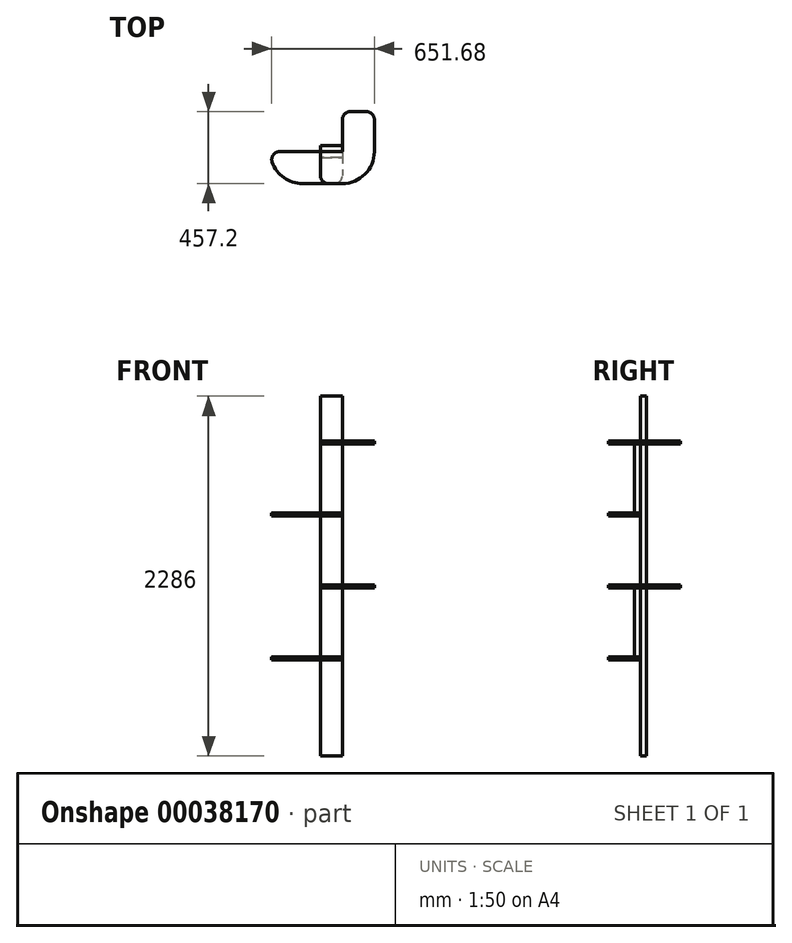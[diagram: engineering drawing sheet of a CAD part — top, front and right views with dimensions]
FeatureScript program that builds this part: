
annotation { "Feature Type Name" : "Feature", "Feature Type Description" : "" }
export const myFeature = defineFeature(function(context is Context, id is Id, definition is map)
    precondition{}
    {
        {
            var Q0;
            Q0=qCreatedBy(makeId("Top.planeOp"),FACE);
            cPlane(context, id + "F0", {"entities" : qUnion([Q0]), "cplaneType" : CPlaneType.OFFSET, "offset" : 609.6 * mm, "width" : 152.4 * mm, "height" : 152.4 * mm});
        }
        {
            var Q0;
            Q0=qCreatedBy(id+"F0.planeOp",FACE);
            cPlane(context, id + "F1", {"entities" : qUnion([Q0]), "cplaneType" : CPlaneType.OFFSET, "offset" : 457.2 * mm, "width" : 152.4 * mm, "height" : 152.4 * mm});
        }
        {
            var Q0;
            Q0=qCreatedBy(id+"F1.planeOp",FACE);
            cPlane(context, id + "F2", {"entities" : qUnion([Q0]), "cplaneType" : CPlaneType.OFFSET, "offset" : 457.2 * mm, "width" : 152.4 * mm, "height" : 152.4 * mm});
        }
        {
            var Q0;
            Q0=qCreatedBy(id+"F2.planeOp",FACE);
            cPlane(context, id + "F3", {"entities" : qUnion([Q0]), "cplaneType" : CPlaneType.OFFSET, "offset" : 457.2 * mm, "width" : 152.4 * mm, "height" : 152.4 * mm});
        }
        {
            var Q0;
            Q0=qCreatedBy(makeId("Top.planeOp"),FACE);
            var sketch = newSketch(context, id + "F4", { "sketchPlane" : qUnion([Q0])});
            skLineSegment(sketch, "E0.bottom", {"start": v(0, 0) * mm, "end": v(-139.7, 0) * mm});
            skLineSegment(sketch, "E0.top", {"start": v(0, 38.1) * mm, "end": v(-139.7, 38.1) * mm});
            skLineSegment(sketch, "E0.left", {"start": v(0, 0) * mm, "end": v(0, 38.1) * mm});
            skLineSegment(sketch, "E0.right", {"start": v(-139.7, 0) * mm, "end": v(-139.7, 38.1) * mm});
            skSolve(sketch);
        }
        {
            var Q0;
            Q0 = qSketchRegion(id + "F4", true);
            extrude(context, id + "F5", {"entities" : qUnion([Q0]), "depth" : 2286 * mm});
        }
        {
            var Q0;
            Q0=qCreatedBy(id+"F0.planeOp",FACE);
            var sketch = newSketch(context, id + "F6", { "sketchPlane" : qUnion([Q0])});
            skLineSegment(sketch, "E1.bottom", {"start": v(0, 0) * mm, "end": v(-254, 0) * mm});
            skLineSegment(sketch, "E1.top", {"start": v(-50.8, -203.2) * mm, "end": v(-254, -203.2) * mm});
            skLineSegment(sketch, "E1.left", {"start": v(0, 0) * mm, "end": v(0, -152.4) * mm});
            skArc(sketch, "E2", {"start": v(-254, -203.2) * mm, "mid": v(-371.32, -165.91) * mm, "end": v(-445.58, -67.73) * mm});
            skLineSegment(sketch, "E3", {"start": v(-397.68, 0) * mm, "end": v(-254, 0) * mm});
            skPoint(sketch, "E4.visualSharp", {"position": v(0, -203.2) * mm});
            skArc(sketch, "E4.filletArc", {"start": v(-50.8, -203.2) * mm, "mid": v(-14.88, -188.32) * mm, "end": v(0, -152.4) * mm});
            skPoint(sketch, "E5.visualSharp", {"position": v(-457.2, 0) * mm});
            skArc(sketch, "E5.filletArc", {"start": v(-397.68, 0) * mm, "mid": v(-439.16, -21.47) * mm, "end": v(-445.58, -67.73) * mm});
            skSolve(sketch);
        }
        {
            var Q0;
            Q0 = qSketchRegion(id + "F6", true);
            extrude(context, id + "F7", {"entities" : qUnion([Q0]), "depth" : 19.05 * mm});
        }
        {
            var Q0;
            Q0=qCreatedBy(id+"F1.planeOp",FACE);
            var sketch = newSketch(context, id + "F8", { "sketchPlane" : qUnion([Q0])});
            skLineSegment(sketch, "E6", {"start": v(-139.7, 0) * mm, "end": v(-139.7, -152.4) * mm});
            skArc(sketch, "E7", {"start": v(-139.7, -152.4) * mm, "mid": v(-124.82, -188.32) * mm, "end": v(-88.9, -203.2) * mm});
            skLineSegment(sketch, "E8", {"start": v(-88.9, -203.2) * mm, "end": v(0, -203.2) * mm});
            skLineSegment(sketch, "E9", {"start": v(203.2, 0) * mm, "end": v(203.2, 203.2) * mm});
            skLineSegment(sketch, "E10", {"start": v(152.4, 254) * mm, "end": v(50.8, 254) * mm});
            skLineSegment(sketch, "E11", {"start": v(0, 203.2) * mm, "end": v(0, 0) * mm});
            skArc(sketch, "E12", {"start": v(0, -203.2) * mm, "mid": v(143.68, -143.68) * mm, "end": v(203.2, 0) * mm});
            skPoint(sketch, "E13.visualSharp", {"position": v(0, 254) * mm});
            skArc(sketch, "E13.filletArc", {"start": v(50.8, 254) * mm, "mid": v(14.88, 239.12) * mm, "end": v(0, 203.2) * mm});
            skPoint(sketch, "E14.visualSharp", {"position": v(203.2, 254) * mm});
            skArc(sketch, "E14.filletArc", {"start": v(203.2, 203.2) * mm, "mid": v(188.32, 239.12) * mm, "end": v(152.4, 254) * mm});
            skLineSegment(sketch, "E15", {"start": v(-139.7, 0) * mm, "end": v(0, 0) * mm});
            skSolve(sketch);
        }
        {
            var Q0;
            Q0 = qSketchRegion(id + "F8", true);
            extrude(context, id + "F9", {"entities" : qUnion([Q0]), "depth" : 19.05 * mm});
        }
        {
            var Q0;
            Q0=qCreatedBy(id+"F2.planeOp",FACE);
            var sketch = newSketch(context, id + "F10", { "sketchPlane" : qUnion([Q0])});
            skLineSegment(sketch, "E16.bottom", {"start": v(0, 0) * mm, "end": v(-254, 0) * mm});
            skLineSegment(sketch, "E16.top", {"start": v(-50.8, -203.2) * mm, "end": v(-254, -203.2) * mm});
            skLineSegment(sketch, "E16.left", {"start": v(0, 0) * mm, "end": v(0, -152.4) * mm});
            skArc(sketch, "E17", {"start": v(-254, -203.2) * mm, "mid": v(-371.32, -165.91) * mm, "end": v(-445.58, -67.73) * mm});
            skLineSegment(sketch, "E18", {"start": v(-397.68, 0) * mm, "end": v(-254, 0) * mm});
            skPoint(sketch, "E19.visualSharp", {"position": v(0, -203.2) * mm});
            skArc(sketch, "E19.filletArc", {"start": v(-50.8, -203.2) * mm, "mid": v(-14.88, -188.32) * mm, "end": v(0, -152.4) * mm});
            skPoint(sketch, "E20.visualSharp", {"position": v(-457.2, 0) * mm});
            skArc(sketch, "E20.filletArc", {"start": v(-397.68, 0) * mm, "mid": v(-439.16, -21.47) * mm, "end": v(-445.58, -67.73) * mm});
            skSolve(sketch);
        }
        {
            var Q0;
            Q0 = qSketchRegion(id + "F10", true);
            extrude(context, id + "F11", {"entities" : qUnion([Q0]), "depth" : 19.05 * mm});
        }
        {
            var Q0;
            Q0=qCreatedBy(id+"F3.planeOp",FACE);
            var sketch = newSketch(context, id + "F12", { "sketchPlane" : qUnion([Q0])});
            skLineSegment(sketch, "E21", {"start": v(-139.7, 0) * mm, "end": v(-139.7, -152.4) * mm});
            skArc(sketch, "E22", {"start": v(-139.7, -152.4) * mm, "mid": v(-124.82, -188.32) * mm, "end": v(-88.9, -203.2) * mm});
            skLineSegment(sketch, "E23", {"start": v(-88.9, -203.2) * mm, "end": v(0, -203.2) * mm});
            skLineSegment(sketch, "E24", {"start": v(203.2, 0) * mm, "end": v(203.2, 203.2) * mm});
            skLineSegment(sketch, "E25", {"start": v(152.4, 254) * mm, "end": v(50.8, 254) * mm});
            skLineSegment(sketch, "E26", {"start": v(0, 203.2) * mm, "end": v(0, 0) * mm});
            skArc(sketch, "E27", {"start": v(0, -203.2) * mm, "mid": v(143.68, -143.68) * mm, "end": v(203.2, 0) * mm});
            skPoint(sketch, "E28.visualSharp", {"position": v(0, 254) * mm});
            skArc(sketch, "E28.filletArc", {"start": v(50.8, 254) * mm, "mid": v(14.88, 239.12) * mm, "end": v(0, 203.2) * mm});
            skPoint(sketch, "E29.visualSharp", {"position": v(203.2, 254) * mm});
            skArc(sketch, "E29.filletArc", {"start": v(203.2, 203.2) * mm, "mid": v(188.32, 239.12) * mm, "end": v(152.4, 254) * mm});
            skLineSegment(sketch, "E30", {"start": v(-139.7, 0) * mm, "end": v(0, 0) * mm});
            skSolve(sketch);
        }
        {
            var Q0;
            Q0 = qSketchRegion(id + "F12", true);
            extrude(context, id + "F13", {"entities" : qUnion([Q0]), "depth" : 19.05 * mm});
        }
        {
            var Q0;
            Q0=makeQuery(id+"F7.opExtrude","CAP_FACE",FACE,{"disambiguationData":[OSD([sQuery(id+"F6.wireOp",EDGE,"E1.bottom"),sQuery(id+"F6.wireOp",EDGE,"E1.top"),sQuery(id+"F6.wireOp",EDGE,"E1.left"),sQuery(id+"F6.wireOp",EDGE,"E2"),sQuery(id+"F6.wireOp",EDGE,"E3"),sQuery(id+"F6.wireOp",EDGE,"E4.filletArc"),sQuery(id+"F6.wireOp",EDGE,"E5.filletArc")])],"isStart":false});
            var sketch = newSketch(context, id + "F14", { "sketchPlane" : qUnion([Q0])});
            skLineSegment(sketch, "E31.bottom", {"start": v(-139.8, 0) * mm, "end": v(0, 0) * mm});
            skLineSegment(sketch, "E31.top", {"start": v(-139.8, -38.1) * mm, "end": v(0, -38.1) * mm});
            skLineSegment(sketch, "E31.left", {"start": v(-139.8, 0) * mm, "end": v(-139.8, -38.1) * mm});
            skLineSegment(sketch, "E31.right", {"start": v(0, 0) * mm, "end": v(0, -38.1) * mm});
            skSolve(sketch);
        }
        {
            var Q0;
            Q0 = qSketchRegion(id + "F14", true);
            var Q1;
            Q1=makeQuery(id+"F9.opExtrude","SWEPT_BODY",BODY,{"disambiguationData":[OSD([sQuery(id+"F8.wireOp",EDGE,"E6"),sQuery(id+"F8.wireOp",EDGE,"E7"),sQuery(id+"F8.wireOp",EDGE,"E8"),sQuery(id+"F8.wireOp",EDGE,"E9"),sQuery(id+"F8.wireOp",EDGE,"E10"),sQuery(id+"F8.wireOp",EDGE,"E11"),sQuery(id+"F8.wireOp",EDGE,"E12"),sQuery(id+"F8.wireOp",EDGE,"E13.filletArc"),sQuery(id+"F8.wireOp",EDGE,"E14.filletArc"),sQuery(id+"F8.wireOp",EDGE,"E15")])]});
            extrude(context, id + "F15", {"entities" : qUnion([Q0]), "endBoundEntityBody" : qUnion([Q1]), "depth" : 438.15 * mm});
        }
        {
            var Q0;
            Q0=makeQuery(id+"F11.opExtrude","CAP_FACE",FACE,{"disambiguationData":[OSD([sQuery(id+"F10.wireOp",EDGE,"E16.bottom"),sQuery(id+"F10.wireOp",EDGE,"E16.top"),sQuery(id+"F10.wireOp",EDGE,"E16.left"),sQuery(id+"F10.wireOp",EDGE,"E17"),sQuery(id+"F10.wireOp",EDGE,"E18"),sQuery(id+"F10.wireOp",EDGE,"E19.filletArc"),sQuery(id+"F10.wireOp",EDGE,"E20.filletArc")])],"isStart":false});
            var sketch = newSketch(context, id + "F16", { "sketchPlane" : qUnion([Q0])});
            skLineSegment(sketch, "E32.bottom", {"start": v(0, 0) * mm, "end": v(-139.7, 0) * mm});
            skLineSegment(sketch, "E32.top", {"start": v(0, -38.1) * mm, "end": v(-139.7, -38.1) * mm});
            skLineSegment(sketch, "E32.left", {"start": v(0, 0) * mm, "end": v(0, -38.1) * mm});
            skLineSegment(sketch, "E32.right", {"start": v(-139.7, 0) * mm, "end": v(-139.7, -38.1) * mm});
            skSolve(sketch);
        }
        {
            var Q0;
            Q0 = qSketchRegion(id + "F16", true);
            extrude(context, id + "F17", {"entities" : qUnion([Q0]), "depth" : 438.15 * mm});
        }
    });
